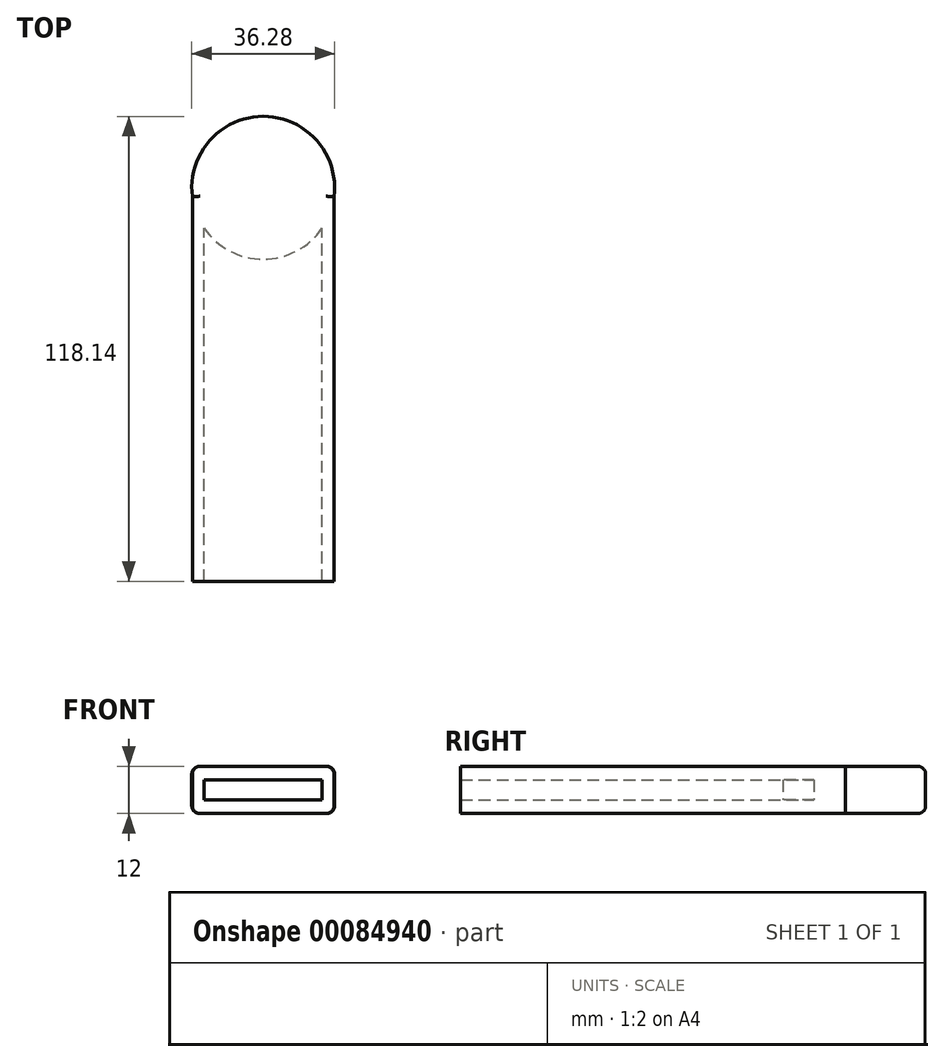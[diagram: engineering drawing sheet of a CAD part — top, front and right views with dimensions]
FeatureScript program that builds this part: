
annotation { "Feature Type Name" : "Feature", "Feature Type Description" : "" }
export const myFeature = defineFeature(function(context is Context, id is Id, definition is map)
    precondition{}
    {
        {
            var Q0;
            Q0=qCreatedBy(makeId("Front.planeOp"),FACE);
            var sketch = newSketch(context, id + "F0", { "sketchPlane" : qUnion([Q0])});
            skLineSegment(sketch, "E0.bottom", {"start": v(-18, 6) * mm, "end": v(18, 6) * mm});
            skLineSegment(sketch, "E0.top", {"start": v(-18, -6) * mm, "end": v(18, -6) * mm});
            skLineSegment(sketch, "E0.left", {"start": v(-18, 6) * mm, "end": v(-18, -6) * mm});
            skLineSegment(sketch, "E0.right", {"start": v(18, 6) * mm, "end": v(18, -6) * mm});
            skPoint(sketch, "E0.middle", {"position": v(0, 0) * mm});
            skLineSegment(sketch, "E1.bottom", {"start": v(-15, 2.5) * mm, "end": v(15, 2.5) * mm});
            skLineSegment(sketch, "E1.top", {"start": v(-15, -2.5) * mm, "end": v(15, -2.5) * mm});
            skLineSegment(sketch, "E1.left", {"start": v(-15, 2.5) * mm, "end": v(-15, -2.5) * mm});
            skLineSegment(sketch, "E1.right", {"start": v(15, 2.5) * mm, "end": v(15, -2.5) * mm});
            skSolve(sketch);
        }
        {
            var Q0;
            Q0=makeQuery(id+"F0.imprint","IMPRINT",FACE,{"disambiguationData":[TD([[makeQuery(id+"F0.imprint","IMPRINT",EDGE,{"derivedFrom":sQuery(id+"F0.wireOp",EDGE,"E0.bottom")}),-1.0]])]});
            extrude(context, id + "F1", {"entities" : qUnion([Q0]), "depth" : 100 * mm});
        }
        {
            var Q0;
            Q0=qCreatedBy(makeId("Top.planeOp"),FACE);
            var sketch = newSketch(context, id + "F2", { "sketchPlane" : qUnion([Q0])});
            skCircle(sketch, "E2", {"center": v(0, 0) * mm, "radius": 18.14 * mm});
            skSolve(sketch);
        }
        {
            var Q0;
            Q0 = qSketchRegion(id + "F2", true);
            extrude(context, id + "F3", {"entities" : qUnion([Q0]), "operationType" : NewBodyOperationType.ADD, "depth" : 6 * mm});
        }
        {
            var Q0;
            Q0=makeQuery(id+"F3.opExtrude","CAP_FACE",FACE,{"disambiguationData":[OSD([sQuery(id+"F2.wireOp",EDGE,"E2")])],"isStart":true});
            extrude(context, id + "F4", {"entities" : qUnion([Q0]), "operationType" : NewBodyOperationType.ADD, "depth" : 6 * mm});
        }
        {
            var Q0;
            Q0=makeQuery(id+"F1.opExtrude","SWEPT_EDGE",EDGE,{"disambiguationData":[OSD([sQuery(id+"F0.wireOp",EDGE,"E0.bottom"),sQuery(id+"F0.wireOp",EDGE,"E0.right")])]});
            var Q1;
            Q1=makeQuery(id+"F3.opExtrude","CAP_EDGE",EDGE,{"disambiguationData":[OSD([sQuery(id+"F2.wireOp",EDGE,"E2")])],"isStart":false});
            var Q2;
            Q2=makeQuery(id+"F1.opExtrude","SWEPT_EDGE",EDGE,{"disambiguationData":[OSD([sQuery(id+"F0.wireOp",EDGE,"E0.bottom"),sQuery(id+"F0.wireOp",EDGE,"E0.left")])]});
            fillet(context, id + "F5", {"entities" : qUnion([Q0, Q1, Q2]), "radius" : 2 * mm, "tangentPropagation" : true, "allowEdgeOverflow" : false});
        }
        {
            var Q0;
            Q0=makeQuery(id+"F1.opExtrude","SWEPT_EDGE",EDGE,{"disambiguationData":[OSD([sQuery(id+"F0.wireOp",EDGE,"E0.top"),sQuery(id+"F0.wireOp",EDGE,"E0.left")])]});
            var Q1;
            {var subQ0=sQuery(id+"F2.wireOp",EDGE,"E2");Q1=makeQuery(id+"F4.opExtrude","CAP_EDGE",EDGE,{"disambiguationData":[OSD([subQ0]),TDD([makeQuery(id+"F3.boolean.opBoolean","SPLIT",EDGE,{"disambiguationData":[TD([makeQuery(id+"F1.opExtrude","SWEPT_FACE",FACE,{"disambiguationData":[OSD([sQuery(id+"F0.wireOp",EDGE,"E0.left")])]})])],"derivedFrom":makeQuery(id+"F3.opExtrude","CAP_EDGE",EDGE,{"disambiguationData":[OSD([subQ0])],"isStart":true})})])],"isStart":false});}
            var Q2;
            Q2=makeQuery(id+"F1.opExtrude","SWEPT_EDGE",EDGE,{"disambiguationData":[OSD([sQuery(id+"F0.wireOp",EDGE,"E0.top"),sQuery(id+"F0.wireOp",EDGE,"E0.right")])]});
            fillet(context, id + "F6", {"entities" : qUnion([Q0, Q1, Q2]), "radius" : 2 * mm, "tangentPropagation" : true, "allowEdgeOverflow" : false});
        }
    });
